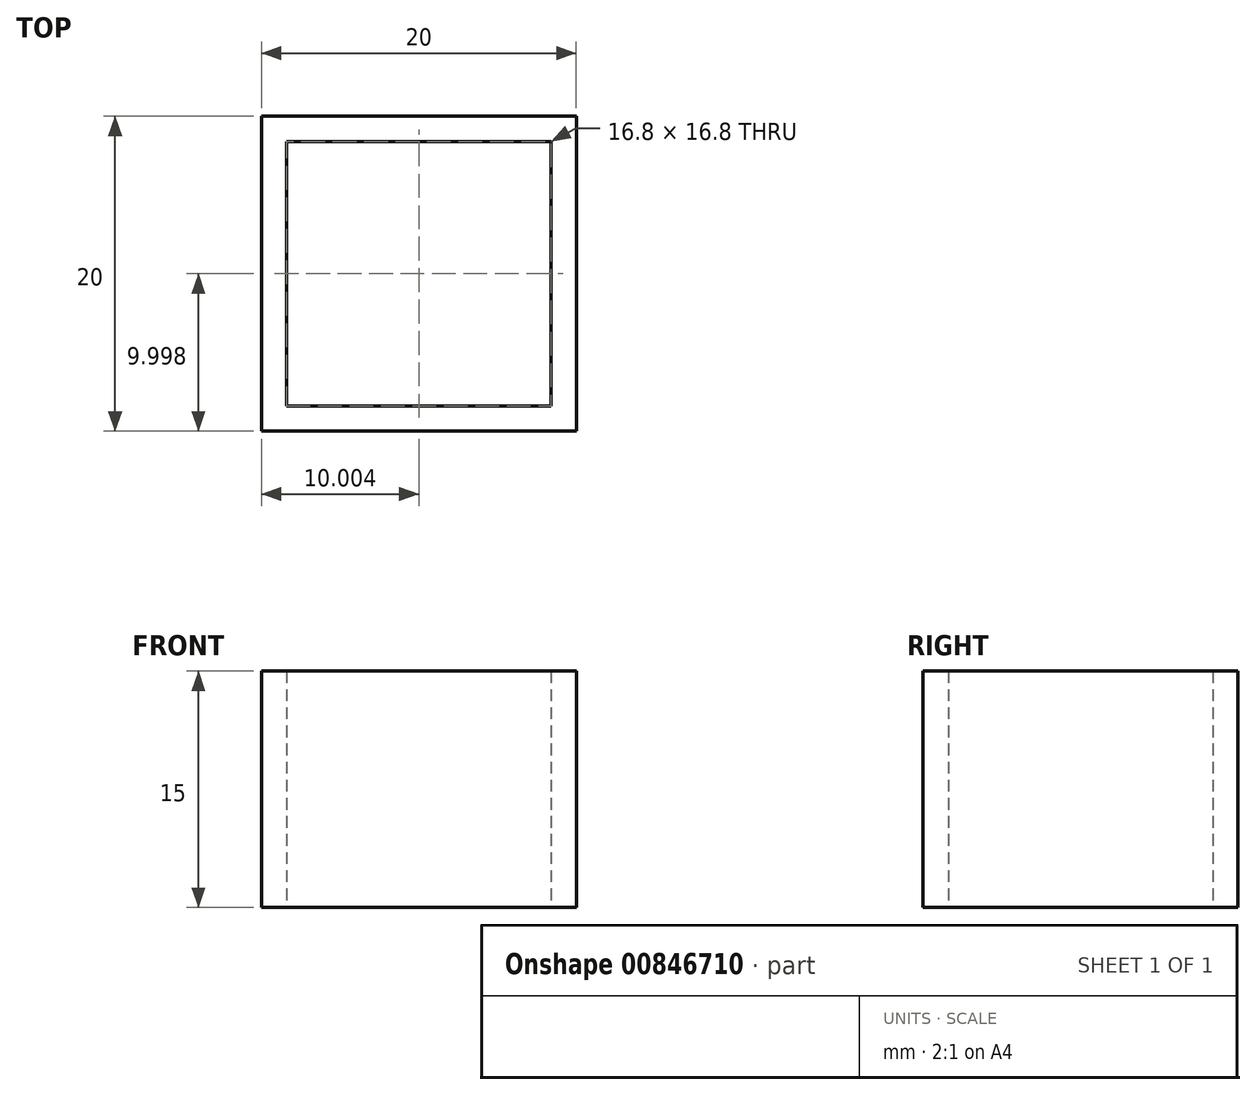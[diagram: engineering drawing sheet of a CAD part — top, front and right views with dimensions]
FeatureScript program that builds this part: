
annotation { "Feature Type Name" : "Feature", "Feature Type Description" : "" }
export const myFeature = defineFeature(function(context is Context, id is Id, definition is map)
    precondition{}
    {
        {
            var Q0;
            Q0=qCreatedBy(makeId("Top.planeOp"),FACE);
            var sketch = newSketch(context, id + "F0", { "sketchPlane" : qUnion([Q0])});
            skLineSegment(sketch, "E0.bottom", {"start": v(10.66, 8.2) * mm, "end": v(30.66, 8.2) * mm});
            skLineSegment(sketch, "E0.top", {"start": v(10.66, -11.8) * mm, "end": v(30.66, -11.8) * mm});
            skLineSegment(sketch, "E0.left", {"start": v(10.66, 8.2) * mm, "end": v(10.66, -11.8) * mm});
            skLineSegment(sketch, "E0.right", {"start": v(30.66, 8.2) * mm, "end": v(30.66, -11.8) * mm});
            skLineSegment(sketch, "E1.0", {"start": v(12.26, -10.2) * mm, "end": v(29.06, -10.2) * mm});
            skLineSegment(sketch, "E1.1", {"start": v(12.26, 6.6) * mm, "end": v(12.26, -10.2) * mm});
            skLineSegment(sketch, "E1.2", {"start": v(12.26, 6.6) * mm, "end": v(29.06, 6.6) * mm});
            skLineSegment(sketch, "E1.3", {"start": v(29.06, 6.6) * mm, "end": v(29.06, -10.2) * mm});
            skSolve(sketch);
        }
        {
            var Q0;
            Q0=makeQuery(id+"F0.imprint","IMPRINT",FACE,{"disambiguationData":[TD([[makeQuery(id+"F0.imprint","IMPRINT",EDGE,{"derivedFrom":sQuery(id+"F0.wireOp",EDGE,"E0.bottom")}),-1.0]])]});
            extrude(context, id + "F1", {"entities" : qUnion([Q0]), "depth" : 15 * mm, "offsetDistance" : 25 * mm});
        }
    });
